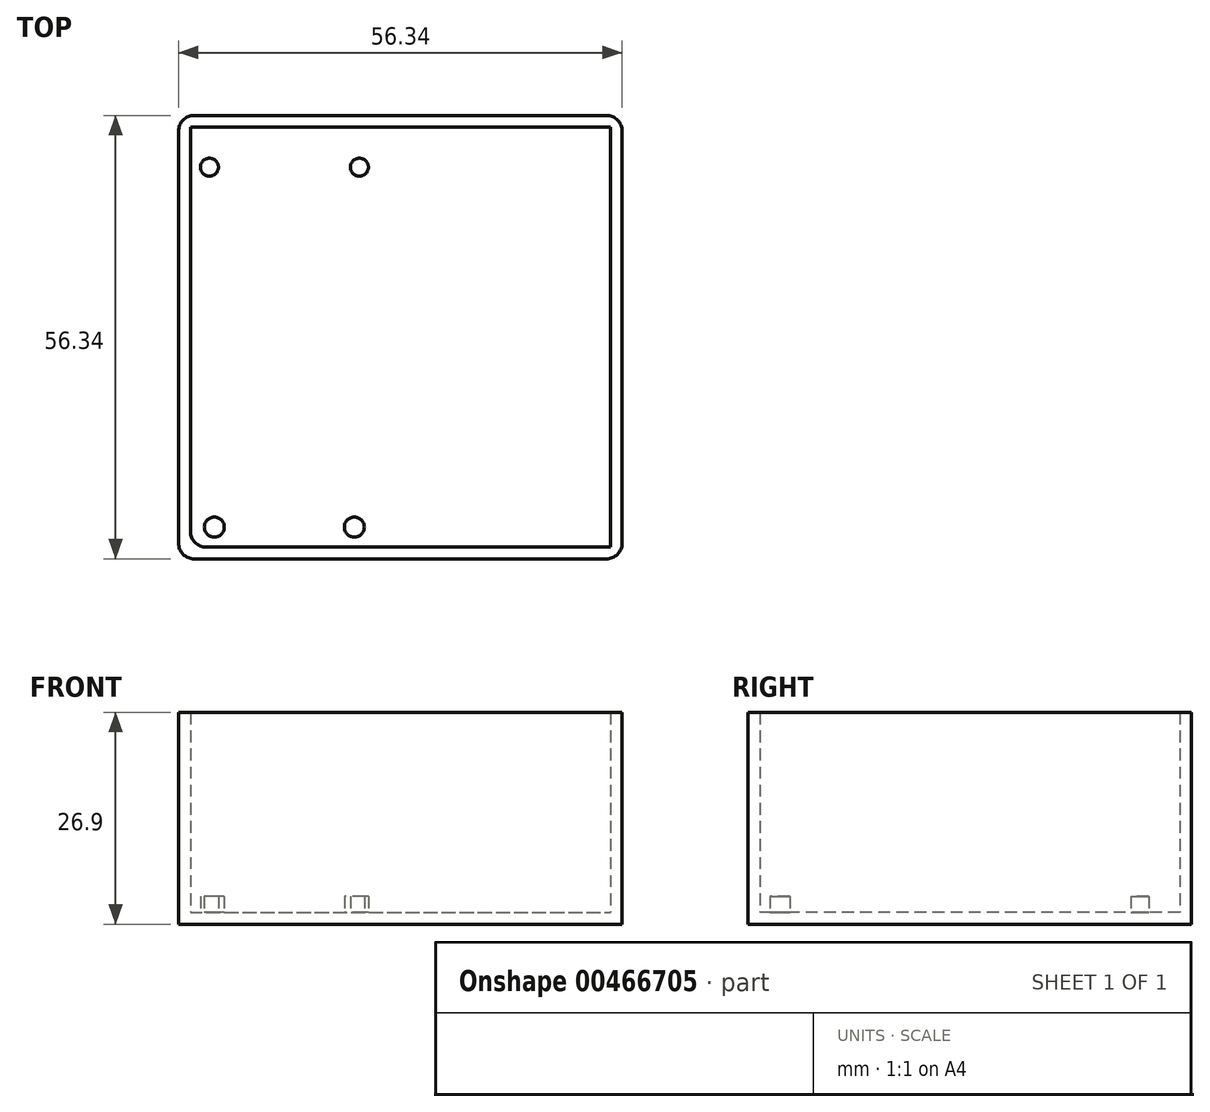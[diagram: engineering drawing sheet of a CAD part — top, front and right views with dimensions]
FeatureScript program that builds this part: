
annotation { "Feature Type Name" : "Feature", "Feature Type Description" : "" }
export const myFeature = defineFeature(function(context is Context, id is Id, definition is map)
    precondition{}
    {
        {
            var Q0;
            Q0=qCreatedBy(makeId("Top.planeOp"),FACE);
            var sketch = newSketch(context, id + "F0", { "sketchPlane" : qUnion([Q0])});
            skLineSegment(sketch, "E0.bottom", {"start": v(-26.67, 26.67) * mm, "end": v(26.67, 26.67) * mm});
            skLineSegment(sketch, "E0.top", {"start": v(-26.67, -26.67) * mm, "end": v(26.67, -26.67) * mm});
            skLineSegment(sketch, "E0.left", {"start": v(-26.67, 26.67) * mm, "end": v(-26.67, -26.67) * mm});
            skLineSegment(sketch, "E0.right", {"start": v(26.67, 26.67) * mm, "end": v(26.67, -26.67) * mm});
            skPoint(sketch, "E0.middle", {"position": v(0, 0) * mm});
            skSolve(sketch);
        }
        {
            var Q0;
            Q0=makeQuery(id+"F0.imprint","IMPRINT",FACE,{"disambiguationData":[TD([[makeQuery(id+"F0.imprint","IMPRINT",EDGE,{"derivedFrom":sQuery(id+"F0.wireOp",EDGE,"E0.bottom")}),-1.0]])]});
            extrude(context, id + "F1", {"entities" : qUnion([Q0]), "depth" : 25.4 * mm, "offsetDistance" : 25 * mm});
        }
        {
            var Q0;
            Q0=makeQuery(id+"F1.opExtrude","CAP_FACE",FACE,{"disambiguationData":[OSD([sQuery(id+"F0.wireOp",EDGE,"E0.bottom"),sQuery(id+"F0.wireOp",EDGE,"E0.top"),sQuery(id+"F0.wireOp",EDGE,"E0.left"),sQuery(id+"F0.wireOp",EDGE,"E0.right")])],"isStart":false});
            shell(context, id + "F2", {"entities" : qUnion([Q0]), "thickness" : 1.5 * mm, "oppositeDirection" : true});
        }
        {
            var Q0;
            Q0=makeQuery(id+"F0.imprint","IMPRINT",FACE,{"disambiguationData":[TD([[makeQuery(id+"F0.imprint","IMPRINT",EDGE,{"derivedFrom":sQuery(id+"F0.wireOp",EDGE,"E0.bottom")}),-1.0]])]});
            var sketch = newSketch(context, id + "F3", { "sketchPlane" : qUnion([Q0])});
            skLineSegment(sketch, "E1.bottom", {"start": v(-24.17, 24.13) * mm, "end": v(-5.31, 24.13) * mm, "construction": true});
            skLineSegment(sketch, "E1.top", {"start": v(-24.17, -26.67) * mm, "end": v(-5.31, -26.67) * mm, "construction": true});
            skLineSegment(sketch, "E1.left", {"start": v(-26.17, 22.13) * mm, "end": v(-26.17, -24.67) * mm, "construction": true});
            skLineSegment(sketch, "E1.right", {"start": v(-3.31, 22.13) * mm, "end": v(-3.31, -24.67) * mm, "construction": true});
            skPoint(sketch, "E1.middle", {"position": v(-14.74, -1.27) * mm});
            skPoint(sketch, "E2.visualSharp", {"position": v(-26.17, 24.13) * mm});
            skArc(sketch, "E2.filletArc", {"start": v(-24.17, 24.13) * mm, "mid": v(-25.58, 23.54) * mm, "end": v(-26.17, 22.13) * mm, "construction": true});
            skPoint(sketch, "E3.visualSharp", {"position": v(-3.31, 24.13) * mm});
            skArc(sketch, "E3.filletArc", {"start": v(-3.31, 22.13) * mm, "mid": v(-3.9, 23.54) * mm, "end": v(-5.31, 24.13) * mm, "construction": true});
            skPoint(sketch, "E4.visualSharp", {"position": v(-3.31, -26.67) * mm});
            skArc(sketch, "E4.filletArc", {"start": v(-5.31, -26.67) * mm, "mid": v(-3.9, -26.08) * mm, "end": v(-3.31, -24.67) * mm, "construction": true});
            skPoint(sketch, "E5.visualSharp", {"position": v(-26.17, -26.67) * mm});
            skArc(sketch, "E5.filletArc", {"start": v(-26.17, -24.67) * mm, "mid": v(-25.58, -26.08) * mm, "end": v(-24.17, -26.67) * mm, "construction": true});
            skCircle(sketch, "E6", {"center": v(-23.63, -24.13) * mm, "radius": 1.27 * mm});
            skCircle(sketch, "E7", {"center": v(-5.85, -24.13) * mm, "radius": 1.27 * mm});
            skCircle(sketch, "E8", {"center": v(-24.25, 21.59) * mm, "radius": 1.14 * mm});
            skCircle(sketch, "E9", {"center": v(-5.2, 21.59) * mm, "radius": 1.14 * mm});
            skSolve(sketch);
        }
        {
            var Q0;
            Q0 = qSketchRegion(id + "F3", true);
            extrude(context, id + "F4", {"entities" : qUnion([Q0]), "operationType" : NewBodyOperationType.ADD, "depth" : 2 * mm, "offsetDistance" : 25 * mm});
        }
        {
            var Q0;
            Q0=makeQuery(id+"F1.opExtrude","SWEPT_EDGE",EDGE,{"disambiguationData":[OSD([sQuery(id+"F0.wireOp",EDGE,"E0.top"),sQuery(id+"F0.wireOp",EDGE,"E0.left")])]});
            var Q1;
            Q1=makeQuery(id+"F1.opExtrude","SWEPT_EDGE",EDGE,{"disambiguationData":[OSD([sQuery(id+"F0.wireOp",EDGE,"E0.bottom"),sQuery(id+"F0.wireOp",EDGE,"E0.left")])]});
            var Q2;
            Q2=makeQuery(id+"F1.opExtrude","SWEPT_EDGE",EDGE,{"disambiguationData":[OSD([sQuery(id+"F0.wireOp",EDGE,"E0.bottom"),sQuery(id+"F0.wireOp",EDGE,"E0.right")])]});
            var Q3;
            Q3=makeQuery(id+"F1.opExtrude","SWEPT_EDGE",EDGE,{"disambiguationData":[OSD([sQuery(id+"F0.wireOp",EDGE,"E0.top"),sQuery(id+"F0.wireOp",EDGE,"E0.right")])]});
            fillet(context, id + "F5", {"entities" : qUnion([Q0, Q1, Q2, Q3]), "radius" : 2 * mm, "tangentPropagation" : true, "allowEdgeOverflow" : false});
        }
        {
            var Q0;
            Q0=makeQuery(id+"F2.opShell","OFFSET_EDGE",EDGE,{"disambiguationData":[OSD([sQuery(id+"F0.wireOp",EDGE,"E0.top"),sQuery(id+"F0.wireOp",EDGE,"E0.left")])]});
            fillet(context, id + "F6", {"entities" : qUnion([Q0]), "radius" : 2 * mm, "tangentPropagation" : true, "allowEdgeOverflow" : false});
        }
    });
